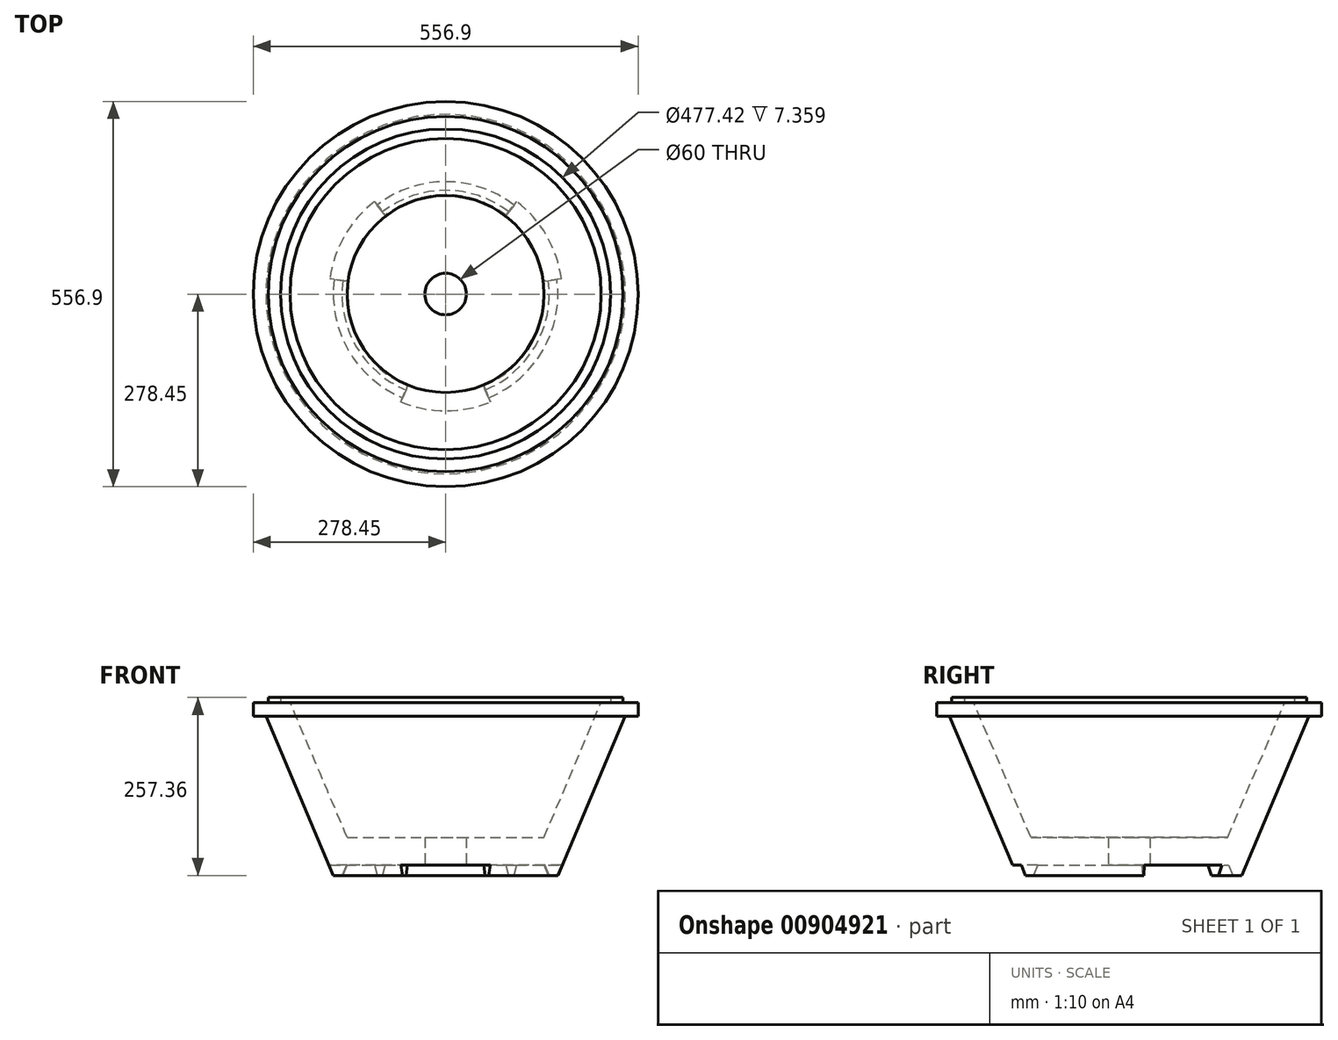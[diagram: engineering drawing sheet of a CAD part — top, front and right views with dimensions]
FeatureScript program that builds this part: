
annotation { "Feature Type Name" : "Feature", "Feature Type Description" : "" }
export const myFeature = defineFeature(function(context is Context, id is Id, definition is map)
    precondition{}
    {
        {
            var Q0;
            Q0=qCreatedBy(makeId("Front.planeOp"),FACE);
            var sketch = newSketch(context, id + "F0", { "sketchPlane" : qUnion([Q0])});
            skLineSegment(sketch, "E0", {"start": v(-142.55, 0) * mm, "end": v(142.55, 0) * mm, "construction": true});
            skPoint(sketch, "E1", {"position": v(0, 0) * mm});
            skLineSegment(sketch, "E2", {"start": v(0, 0) * mm, "end": v(0, 77.71) * mm, "construction": true});
            skLineSegment(sketch, "E3", {"start": v(30, 15) * mm, "end": v(30, 55) * mm});
            skLineSegment(sketch, "E4", {"start": v(30, 55) * mm, "end": v(142.34, 55) * mm});
            skLineSegment(sketch, "E5", {"start": v(30, 15) * mm, "end": v(143.64, 15) * mm});
            skLineSegment(sketch, "E6", {"start": v(143.64, 15) * mm, "end": v(150, 0) * mm});
            skLineSegment(sketch, "E7", {"start": v(150, 0) * mm, "end": v(162.47, 0) * mm});
            skLineSegment(sketch, "E8", {"start": v(162.47, 0) * mm, "end": v(268.45, 250) * mm});
            skLineSegment(sketch, "E9", {"start": v(225, 250) * mm, "end": v(142.34, 55) * mm});
            skLineSegment(sketch, "E10", {"start": v(225, 250) * mm, "end": v(238.71, 250) * mm});
            skLineSegment(sketch, "E11", {"start": v(238.71, 250) * mm, "end": v(238.71, 257.36) * mm});
            skLineSegment(sketch, "E12", {"start": v(238.71, 257.36) * mm, "end": v(256.75, 257.36) * mm});
            skLineSegment(sketch, "E13", {"start": v(256.75, 257.36) * mm, "end": v(256.75, 250) * mm});
            skLineSegment(sketch, "E14", {"start": v(256.75, 250) * mm, "end": v(268.45, 250) * mm});
            skLineSegment(sketch, "E15", {"start": v(225, 250) * mm, "end": v(261.83, 234.39) * mm, "construction": true});
            skLineSegment(sketch, "E16", {"start": v(143.64, 15) * mm, "end": v(168.83, 15) * mm, "construction": true});
            skLineSegment(sketch, "E17", {"start": v(156.23, 15) * mm, "end": v(156.23, 0) * mm, "construction": true});
            skLineSegment(sketch, "E18", {"start": v(225, 250) * mm, "end": v(268.45, 250) * mm, "construction": true});
            skLineSegment(sketch, "E19", {"start": v(246.72, 250) * mm, "end": v(140.75, 0) * mm, "construction": true});
            skLineSegment(sketch, "E20", {"start": v(259.97, 230) * mm, "end": v(278.45, 230) * mm});
            skLineSegment(sketch, "E21", {"start": v(278.45, 230) * mm, "end": v(278.45, 250) * mm});
            skLineSegment(sketch, "E22", {"start": v(278.45, 250) * mm, "end": v(268.45, 250) * mm});
            skSolve(sketch);
        }
        {
            var Q0;
            Q0=makeQuery(id+"F0.imprint","IMPRINT",FACE,{"disambiguationData":[TD([[makeQuery(id+"F0.imprint","IMPRINT",EDGE,{"derivedFrom":sQuery(id+"F0.wireOp",EDGE,"E3")}),-1.0]])]});
            var Q1;
            {var subQ2=sQuery(id+"F0.wireOp",EDGE,"E20");Q1=makeQuery(id+"F0.imprint","IMPRINT",FACE,{"disambiguationData":[TD([[makeQuery(id+"F0.imprint","IMPRINT",EDGE,{"derivedFrom":subQ2}),1.0]])]});}
            var Q2;
            Q2=sQuery(id+"F0.wireOp",EDGE,"E2");
            revolve(context, id + "F1", {"surfaceOperationType" : NewSurfaceOperationType.NEW, "entities" : qUnion([Q0, Q1]), "axis" : qUnion([Q2]), "revolveType" : RevolveType.FULL});
        }
        {
            var Q0;
            Q0=makeQuery(id+"F1.opRevolve","SWEPT_FACE",FACE,{"disambiguationData":[OSD([sQuery(id+"F0.wireOp",EDGE,"E7")])]});
            var sketch = newSketch(context, id + "F2", { "sketchPlane" : qUnion([Q0])});
            skLineSegment(sketch, "E23", {"start": v(0, 0) * mm, "end": v(-82.53, 199.24) * mm});
            skLineSegment(sketch, "E24", {"start": v(-82.53, 199.24) * mm, "end": v(82.53, 199.24) * mm});
            skLineSegment(sketch, "E25", {"start": v(82.53, 199.24) * mm, "end": v(0, 0) * mm});
            skLineSegment(sketch, "E26", {"start": v(0, 0) * mm, "end": v(0, 199.24) * mm, "construction": true});
            skLineSegment(sketch, "E27.1.0", {"start": v(-131.29, -171.1) * mm, "end": v(-213.82, -28.15) * mm});
            skLineSegment(sketch, "E27.1.1", {"start": v(-213.82, -28.15) * mm, "end": v(0, 0) * mm});
            skLineSegment(sketch, "E27.1.2", {"start": v(0, 0) * mm, "end": v(-131.29, -171.1) * mm});
            skLineSegment(sketch, "E27.2.0", {"start": v(213.82, -28.15) * mm, "end": v(131.29, -171.1) * mm});
            skLineSegment(sketch, "E27.2.1", {"start": v(131.29, -171.1) * mm, "end": v(0, 0) * mm});
            skLineSegment(sketch, "E27.2.2", {"start": v(0, 0) * mm, "end": v(213.82, -28.15) * mm});
            skPoint(sketch, "E27.center", {"position": v(0, 0) * mm});
            skSolve(sketch);
        }
        {
            var Q0;
            {var subQ0=sQuery(id+"F2.wireOp",EDGE,"E23");var subQ1=sQuery(id+"F0.wireOp",EDGE,"E7");var subQ2=makeQuery(id+"F1.opRevolve","SWEPT_EDGE",EDGE,{"disambiguationData":[OSD([subQ1,sQuery(id+"F0.wireOp",EDGE,"E8")])]});var subQ3=makeQuery(id+"F2.imprint","INTERSECT",VERTEX,{"derivedFrom":[subQ2,subQ0]});Q0=makeQuery(id+"F2.imprint","IMPRINT",FACE,{"disambiguationData":[TD([[makeQuery(id+"F2.imprint","IMPRINT",EDGE,{"disambiguationData":[TD([[subQ3,1.0]])],"derivedFrom":subQ0}),-1.0]])]});}
            var Q1;
            {var subQ0=sQuery(id+"F0.wireOp",EDGE,"E7");var subQ1=makeQuery(id+"F1.opRevolve","SWEPT_EDGE",EDGE,{"disambiguationData":[OSD([subQ0,sQuery(id+"F0.wireOp",EDGE,"E8")])]});var subQ3=sQuery(id+"F2.wireOp",EDGE,"E27.2.1");var subQ4=makeQuery(id+"F2.imprint","INTERSECT",VERTEX,{"derivedFrom":[subQ1,subQ3]});Q1=makeQuery(id+"F2.imprint","IMPRINT",FACE,{"disambiguationData":[TD([[makeQuery(id+"F2.imprint","IMPRINT",EDGE,{"disambiguationData":[TD([[subQ4,-1.0]])],"derivedFrom":subQ3}),-1.0]])]});}
            var Q2;
            {var subQ0=sQuery(id+"F0.wireOp",EDGE,"E7");var subQ1=makeQuery(id+"F1.opRevolve","SWEPT_EDGE",EDGE,{"disambiguationData":[OSD([subQ0,sQuery(id+"F0.wireOp",EDGE,"E8")])]});var subQ3=sQuery(id+"F2.wireOp",EDGE,"E27.1.1");var subQ4=makeQuery(id+"F2.imprint","INTERSECT",VERTEX,{"derivedFrom":[subQ1,subQ3]});Q2=makeQuery(id+"F2.imprint","IMPRINT",FACE,{"disambiguationData":[TD([[makeQuery(id+"F2.imprint","IMPRINT",EDGE,{"disambiguationData":[TD([[subQ4,-1.0]])],"derivedFrom":subQ3}),-1.0]])]});}
            var Q3;
            {var subQ1=sQuery(id+"F2.wireOp",EDGE,"E27.1.1");var subQ3=makeQuery(id+"F1.opRevolve","SWEPT_EDGE",EDGE,{"disambiguationData":[OSD([sQuery(id+"F0.wireOp",EDGE,"E6"),sQuery(id+"F0.wireOp",EDGE,"E7")])]});var subQ4=makeQuery(id+"F2.imprint","INTERSECT",VERTEX,{"derivedFrom":[subQ3,subQ1]});Q3=makeQuery(id+"F2.imprint","IMPRINT",FACE,{"disambiguationData":[TD([[makeQuery(id+"F2.imprint","IMPRINT",EDGE,{"disambiguationData":[TD([[subQ4,-1.0]])],"derivedFrom":subQ3}),1.0]])]});}
            var Q4;
            {var subQ1=sQuery(id+"F2.wireOp",EDGE,"E23");var subQ3=makeQuery(id+"F1.opRevolve","SWEPT_EDGE",EDGE,{"disambiguationData":[OSD([sQuery(id+"F0.wireOp",EDGE,"E6"),sQuery(id+"F0.wireOp",EDGE,"E7")])]});var subQ4=makeQuery(id+"F2.imprint","INTERSECT",VERTEX,{"derivedFrom":[subQ3,subQ1]});Q4=makeQuery(id+"F2.imprint","IMPRINT",FACE,{"disambiguationData":[TD([[makeQuery(id+"F2.imprint","IMPRINT",EDGE,{"disambiguationData":[TD([[subQ4,1.0]])],"derivedFrom":subQ3}),1.0]])]});}
            var Q5;
            {var subQ1=sQuery(id+"F2.wireOp",EDGE,"E27.2.1");var subQ3=makeQuery(id+"F1.opRevolve","SWEPT_EDGE",EDGE,{"disambiguationData":[OSD([sQuery(id+"F0.wireOp",EDGE,"E6"),sQuery(id+"F0.wireOp",EDGE,"E7")])]});var subQ4=makeQuery(id+"F2.imprint","INTERSECT",VERTEX,{"derivedFrom":[subQ3,subQ1]});Q5=makeQuery(id+"F2.imprint","IMPRINT",FACE,{"disambiguationData":[TD([[makeQuery(id+"F2.imprint","IMPRINT",EDGE,{"disambiguationData":[TD([[subQ4,-1.0]])],"derivedFrom":subQ3}),1.0]])]});}
            var Q6;
            {var subQ0=sQuery(id+"F2.wireOp",EDGE,"E24");Q6=makeQuery(id+"F2.imprint","IMPRINT",FACE,{"disambiguationData":[TD([[makeQuery(id+"F2.imprint","IMPRINT",EDGE,{"derivedFrom":subQ0}),-1.0]])]});}
            var Q7;
            {var subQ0=sQuery(id+"F2.wireOp",EDGE,"E27.1.0");Q7=makeQuery(id+"F2.imprint","IMPRINT",FACE,{"disambiguationData":[TD([[makeQuery(id+"F2.imprint","IMPRINT",EDGE,{"derivedFrom":subQ0}),-1.0]])]});}
            var Q8;
            {var subQ0=sQuery(id+"F2.wireOp",EDGE,"E27.2.0");Q8=makeQuery(id+"F2.imprint","IMPRINT",FACE,{"disambiguationData":[TD([[makeQuery(id+"F2.imprint","IMPRINT",EDGE,{"derivedFrom":subQ0}),-1.0]])]});}
            var Q9;
            Q9=makeQuery(id+"F1.opRevolve","SWEPT_FACE",FACE,{"disambiguationData":[OSD([sQuery(id+"F0.wireOp",EDGE,"E5")])]});
            extrude(context, id + "F3", {"entities" : qUnion([Q0, Q1, Q2, Q3, Q4, Q5, Q6, Q7, Q8]), "operationType" : NewBodyOperationType.REMOVE, "endBound" : BoundingType.UP_TO_SURFACE, "oppositeDirection" : true, "depth" : 25 * mm, "endBoundEntityFace" : qUnion([Q9]), "offsetDistance" : 25 * mm});
        }
    });
